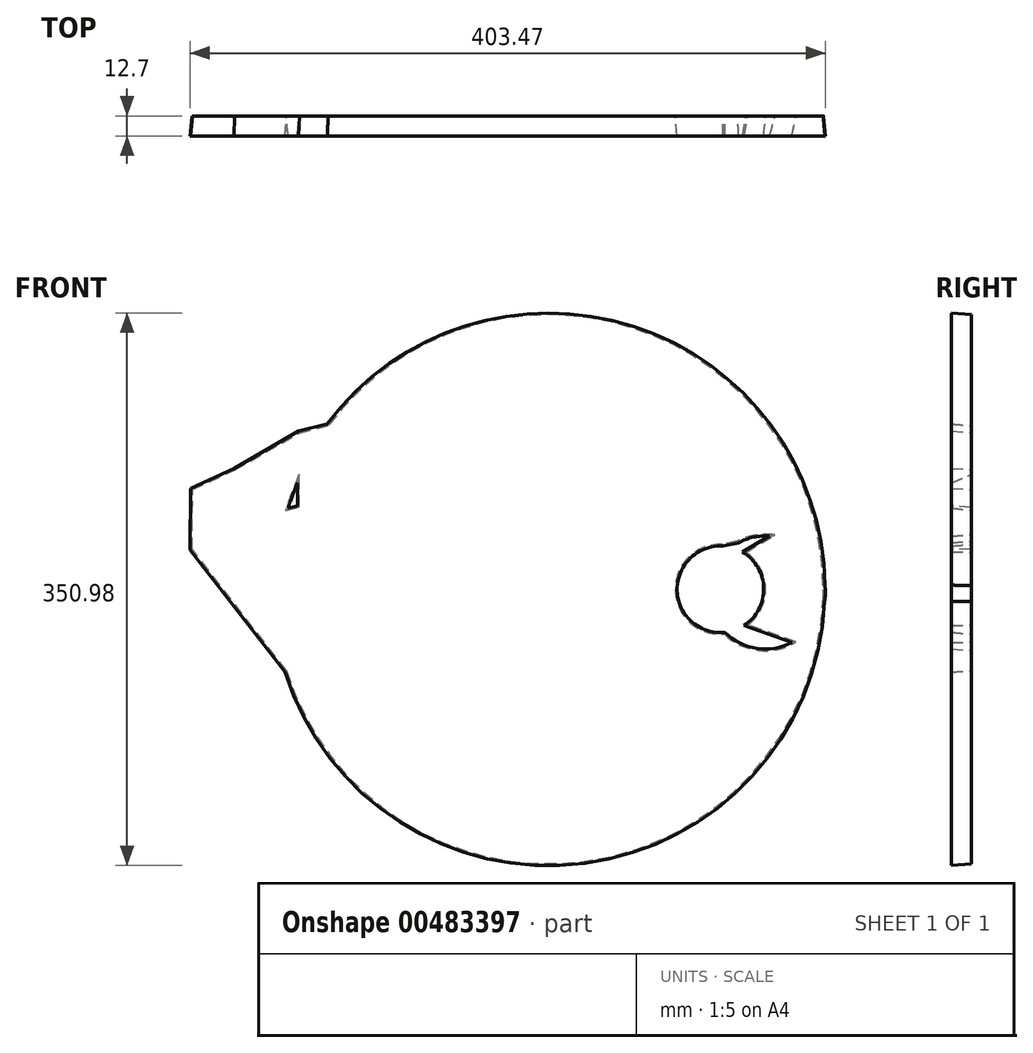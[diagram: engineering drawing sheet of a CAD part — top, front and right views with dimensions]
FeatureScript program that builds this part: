
annotation { "Feature Type Name" : "Feature", "Feature Type Description" : "" }
export const myFeature = defineFeature(function(context is Context, id is Id, definition is map)
    precondition{}
    {
        {
            var Q0;
            Q0=qCreatedBy(makeId("Front.planeOp"),FACE);
            var sketch = newSketch(context, id + "F0", { "sketchPlane" : qUnion([Q0])});
            skCircle(sketch, "E0", {"center": v(0, 0) * mm, "radius": 174.38 * mm});
            skCircle(sketch, "E1", {"center": v(109.08, 0) * mm, "radius": 28.6 * mm});
            skCircle(sketch, "E2", {"center": v(137.61, -2.05) * mm, "radius": 37.03 * mm});
            skLineSegment(sketch, "E3", {"start": v(0, 174.38) * mm, "end": v(108.4, 28.6) * mm});
            skLineSegment(sketch, "E4", {"start": v(108.47, 30.63) * mm, "end": v(131.52, 34.48) * mm});
            skLineSegment(sketch, "E5", {"start": v(0, -174.38) * mm, "end": v(126.88, -61.23) * mm});
            skLineSegment(sketch, "E6", {"start": v(165.56, -36.56) * mm, "end": v(102.6, -14.14) * mm});
            skLineSegment(sketch, "E7", {"start": v(102.6, -14.14) * mm, "end": v(102.6, 10.04) * mm});
            skLineSegment(sketch, "E8", {"start": v(102.6, 10.04) * mm, "end": v(143.7, 34.48) * mm});
            skCircle(sketch, "E9.cCircle", {"center": v(-215.48, 44.28) * mm, "radius": 10.91 * mm, "construction": true});
            skLineSegment(sketch, "E9.0", {"start": v(-193.66, 44.04) * mm, "end": v(-226.6, 25.5) * mm});
            skLineSegment(sketch, "E9.1", {"start": v(-226.6, 25.5) * mm, "end": v(-226.18, 63.3) * mm});
            skLineSegment(sketch, "E9.2", {"start": v(-226.18, 63.3) * mm, "end": v(-193.66, 44.04) * mm});
            skPoint(sketch, "E9.0.midPoint", {"position": v(-210.13, 34.77) * mm});
            skCircle(sketch, "E10.cCircle", {"center": v(-172.09, 75.79) * mm, "radius": 13.66 * mm, "construction": true});
            skLineSegment(sketch, "E10.0", {"start": v(-158.35, 99.41) * mm, "end": v(-158.5, 52.08) * mm});
            skLineSegment(sketch, "E10.1", {"start": v(-158.5, 52.08) * mm, "end": v(-199.41, 75.88) * mm});
            skLineSegment(sketch, "E10.2", {"start": v(-199.41, 75.88) * mm, "end": v(-158.35, 99.41) * mm});
            skPoint(sketch, "E10.0.midPoint", {"position": v(-158.43, 75.75) * mm});
            skLineSegment(sketch, "E11", {"start": v(-226.18, 63.3) * mm, "end": v(-199.41, 75.88) * mm});
            skLineSegment(sketch, "E12", {"start": v(-193.66, 44.04) * mm, "end": v(-158.5, 52.08) * mm});
            skLineSegment(sketch, "E13", {"start": v(-158.35, 99.41) * mm, "end": v(-139.97, 104) * mm});
            skLineSegment(sketch, "E14", {"start": v(-226.6, 25.5) * mm, "end": v(-166.46, -51.96) * mm});
            skLineSegment(sketch, "E15", {"start": v(126.88, -61.23) * mm, "end": v(103.9, -28.13) * mm});
            skLineSegment(sketch, "E16", {"start": v(103.9, -28.13) * mm, "end": v(113.63, -28.24) * mm});
            skLineSegment(sketch, "E17", {"start": v(96.13, 25.5) * mm, "end": v(120.2, 30.63) * mm});
            skSolve(sketch);
        }
        {
            var Q0;
            Q0 = qSketchRegion(id + "F0", true);
            extrude(context, id + "F1", {"entities" : qUnion([Q0]), "depth" : 12.7 * mm, "hasDraft" : true, "draftAngle" : 5 * degree});
        }
    });
